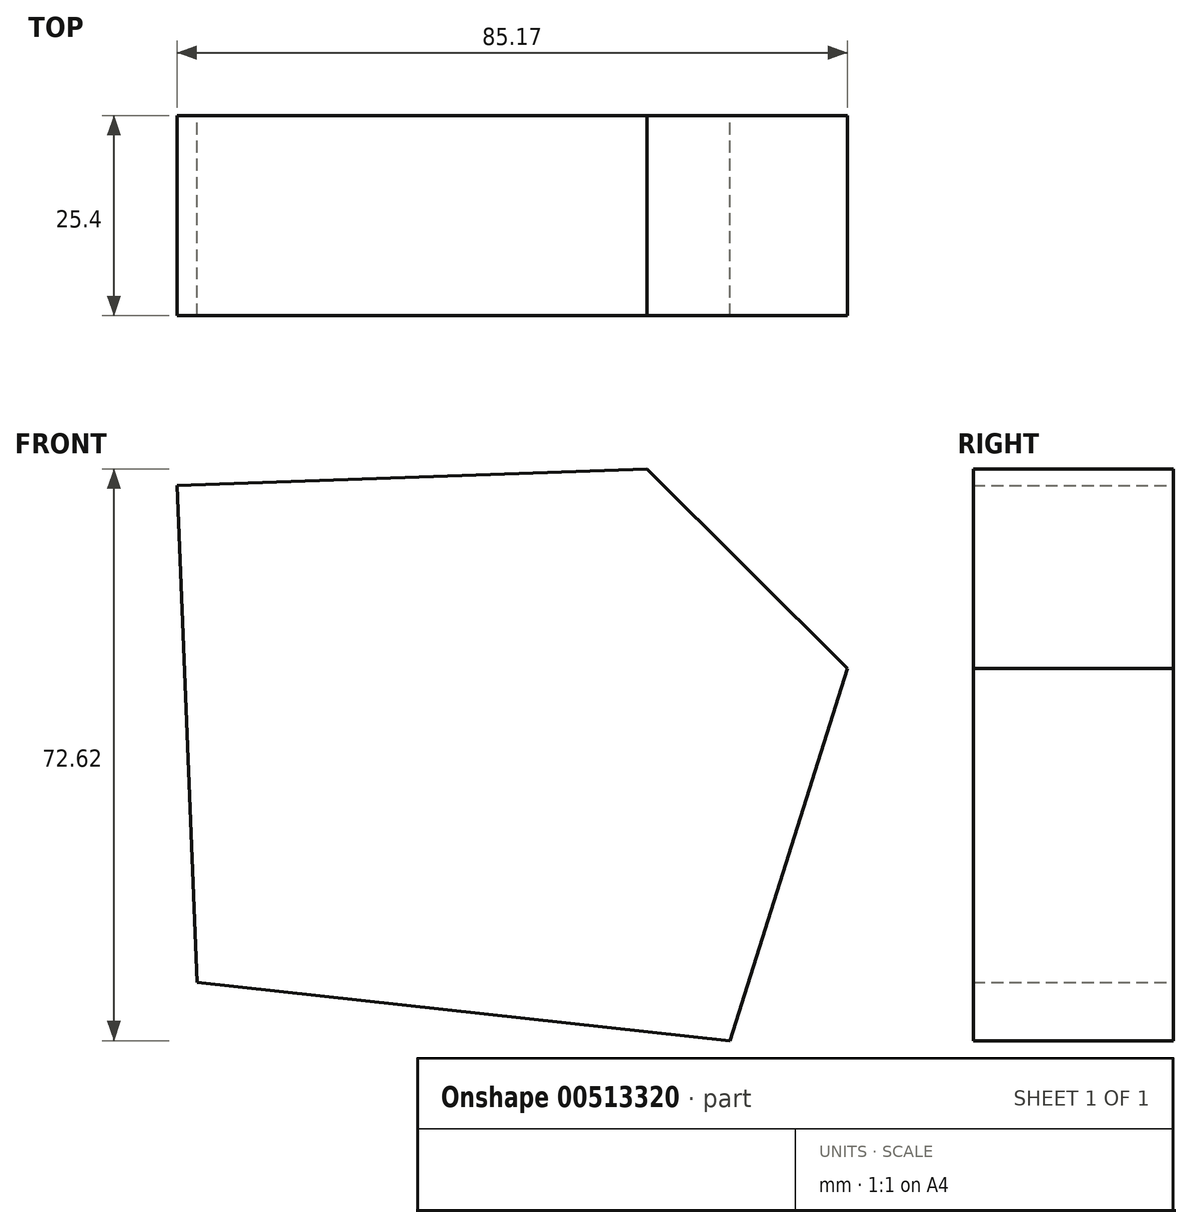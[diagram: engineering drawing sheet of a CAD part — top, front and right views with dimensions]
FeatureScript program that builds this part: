
annotation { "Feature Type Name" : "Feature", "Feature Type Description" : "" }
export const myFeature = defineFeature(function(context is Context, id is Id, definition is map)
    precondition{}
    {
        {
            var Q0;
            Q0=qCreatedBy(makeId("Front.planeOp"),FACE);
            var sketch = newSketch(context, id + "F0", { "sketchPlane" : qUnion([Q0])});
            skLineSegment(sketch, "E0", {"start": v(-48.8, 51.15) * mm, "end": v(10.91, 53.26) * mm});
            skLineSegment(sketch, "E1", {"start": v(10.91, 53.26) * mm, "end": v(36.37, 27.92) * mm});
            skLineSegment(sketch, "E2", {"start": v(36.37, 27.92) * mm, "end": v(21.47, -19.36) * mm});
            skLineSegment(sketch, "E3", {"start": v(21.47, -19.36) * mm, "end": v(-46.22, -11.97) * mm});
            skLineSegment(sketch, "E4", {"start": v(-46.22, -11.97) * mm, "end": v(-48.8, 51.15) * mm});
            skSolve(sketch);
        }
        {
            var Q0;
            Q0=makeQuery(id+"F0.imprint","IMPRINT",FACE,{"disambiguationData":[TD([[makeQuery(id+"F0.imprint","IMPRINT",EDGE,{"derivedFrom":sQuery(id+"F0.wireOp",EDGE,"E0")}),-1.0]])]});
            extrude(context, id + "F1", {"entities" : qUnion([Q0]), "depth" : 25.4 * mm});
        }
    });
